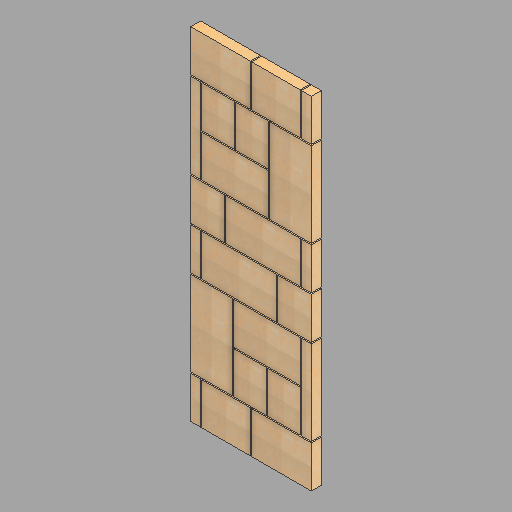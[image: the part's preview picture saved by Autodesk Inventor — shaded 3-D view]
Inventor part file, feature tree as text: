
AUTODESK INVENTOR PART (.ipt)
format: ipt  version: 2022.2 (Build 262287010, 287A)  size: 416,768 bytes
history: native  units: in
note: dims shown in document units (in); Inventor stores cm internally (conversion verified against a paired STEP export)
features: extrude x22, sketch x1
ambient origin geometry x8: Origin, YZ Plane, XZ Plane, XY Plane, X Axis, Y Axis, Z Axis, Center Point
bodies: Body1 (feature_tree), Body2 (feature_tree), Body3 (feature_tree), Body4 (feature_tree), Body5 (feature_tree), Body6 (feature_tree), Body7 (feature_tree), Body8 (feature_tree), Body9 (feature_tree), Body10 (feature_tree), Body11 (feature_tree), Body12 (feature_tree), Body13 (feature_tree), Body14 (feature_tree), Body15 (feature_tree), Body16 (feature_tree), Body17 (feature_tree), Body18 (feature_tree), Body19 (feature_tree), Body20 (feature_tree), Body21 (feature_tree), Body22 (feature_tree)
feature tree (23):
  sketch  "Sketch1"  dims[d0=138.5in d1=48.5in d3=0.5in d4=16.75in d5=0.5in d6=16.75in d7=0.5in d8=16.75in d9=0.5in d10=16.75in d11=0.5in d12=16.75in d13=0.5in d14=16.75in d15=0.5in d16=0.5in d17=16.75in d18=0.5in d19=4.0in d20=4.0in d21=4.0in d22=4.0in d25=16.75in d26=0.5in d27=0.5in d28=0.5in d30=16.75in d31=0.5in d32=16.75in d34=0.5in d35=4.0in d36=0.5in d37=4.0in d38=0.5in d39=4.0in d40=0.5in d46=24.0in d47=19.5in d48=19.5in d49=24.0in d50=13.125in d51=0.5in d52=13.125in d53=0.5in d55=30.0in d56=0.5in d57=30.0in d58=0.5in d59=4.0in d60=0.0in d61=4.0in d62=0.0in d63=4.0in d64=0.0in d65=4.0in d66=0.0in d67=4.0in d68=0.0in d69=4.0in d70=0.0in d71=4.0in d72=0.0in d73=4.0in d74=0.0in d75=4.0in d76=0.0in d77=4.0in d78=0.0in d79=4.0in d80=0.0in d81=4.0in d82=0.0in d83=4.0in d84=0.0in d85=4.0in d86=0.0in d87=4.0in d88=0.0in d89=4.0in d90=0.0in d91=4.0in d92=0.0in d93=4.0in d94=0.0in d95=4.0in d96=0.0in d97=4.0in d98=0.0in d99=4.0in d100=0.0in d101=4.0in d102=0.0in]
  extrude  "Extrusion1"  Depth=48.5in
  extrude  "Extrusion2"  Depth=0.5in
  extrude  "Extrusion3"  Depth=16.75in
  extrude  "Extrusion4"  Depth=0.5in
  extrude  "Extrusion5"  Depth=16.75in
  extrude  "Extrusion6"  Depth=0.5in
  extrude  "Extrusion7"  Depth=16.75in
  extrude  "Extrusion8"  Depth=0.5in
  extrude  "Extrusion9"  Depth=16.75in
  extrude  "Extrusion10"  Depth=0.5in
  extrude  "Extrusion11"  Depth=16.75in
  extrude  "Extrusion12"  Depth=0.5in
  extrude  "Extrusion13"  Depth=16.75in
  extrude  "Extrusion14"  Depth=0.5in
  extrude  "Extrusion15"  Depth=0.5in
  extrude  "Extrusion16"  Depth=16.75in
  extrude  "Extrusion17"  Depth=0.5in
  extrude  "Extrusion18"  Depth=4.0in
  extrude  "Extrusion19"  Depth=4.0in
  extrude  "Extrusion20"  Depth=4.0in
  extrude  "Extrusion21"  Depth=4.0in
  extrude  "Extrusion22"  Depth=16.75in
